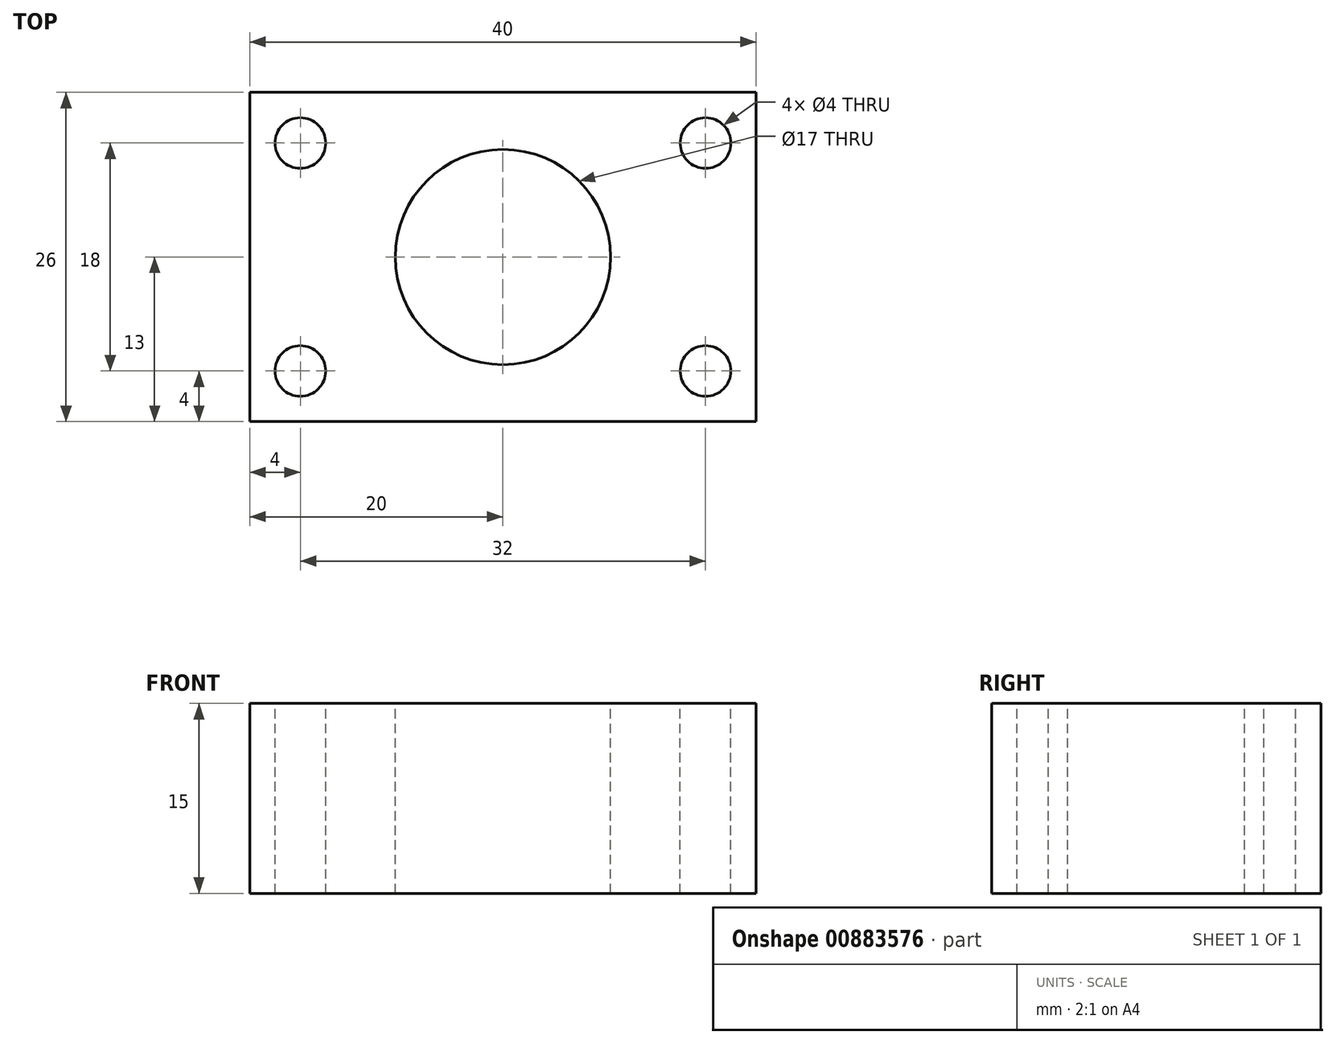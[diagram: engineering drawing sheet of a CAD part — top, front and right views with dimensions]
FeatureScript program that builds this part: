
annotation { "Feature Type Name" : "Feature", "Feature Type Description" : "" }
export const myFeature = defineFeature(function(context is Context, id is Id, definition is map)
    precondition{}
    {
        {
            var Q0;
            Q0=qCreatedBy(makeId("Top.planeOp"),FACE);
            var sketch = newSketch(context, id + "F0", { "sketchPlane" : qUnion([Q0])});
            skLineSegment(sketch, "E0.bottom", {"start": v(-20, 13) * mm, "end": v(20, 13) * mm});
            skLineSegment(sketch, "E0.top", {"start": v(-20, -13) * mm, "end": v(20, -13) * mm});
            skLineSegment(sketch, "E0.left", {"start": v(-20, 13) * mm, "end": v(-20, -13) * mm});
            skLineSegment(sketch, "E0.right", {"start": v(20, 13) * mm, "end": v(20, -13) * mm});
            skSolve(sketch);
        }
        {
            var Q0;
            Q0 = qSketchRegion(id + "F0", true);
            extrude(context, id + "F1", {"entities" : qUnion([Q0]), "depth" : 15 * mm, "offsetDistance" : 25 * mm});
        }
        {
            var Q0;
            Q0=makeQuery(id+"F1.opExtrude","CAP_FACE",FACE,{"disambiguationData":[OSD([sQuery(id+"F0.wireOp",EDGE,"E0.bottom"),sQuery(id+"F0.wireOp",EDGE,"E0.top"),sQuery(id+"F0.wireOp",EDGE,"E0.left"),sQuery(id+"F0.wireOp",EDGE,"E0.right")])],"isStart":false});
            var sketch = newSketch(context, id + "F2", { "sketchPlane" : qUnion([Q0])});
            skCircle(sketch, "E1", {"center": v(0, 0) * mm, "radius": 8.5 * mm});
            skCircle(sketch, "E2", {"center": v(-16, 9) * mm, "radius": 2 * mm});
            skCircle(sketch, "E3", {"center": v(-16, -9) * mm, "radius": 2 * mm});
            skCircle(sketch, "E4", {"center": v(16, 9) * mm, "radius": 2 * mm});
            skCircle(sketch, "E5", {"center": v(16, -9) * mm, "radius": 2 * mm});
            skSolve(sketch);
        }
        {
            var Q0;
            Q0 = qSketchRegion(id + "F2", true);
            extrude(context, id + "F3", {"entities" : qUnion([Q0]), "operationType" : NewBodyOperationType.REMOVE, "endBound" : BoundingType.THROUGH_ALL, "oppositeDirection" : true, "depth" : 25 * mm, "offsetDistance" : 25 * mm});
        }
    });
